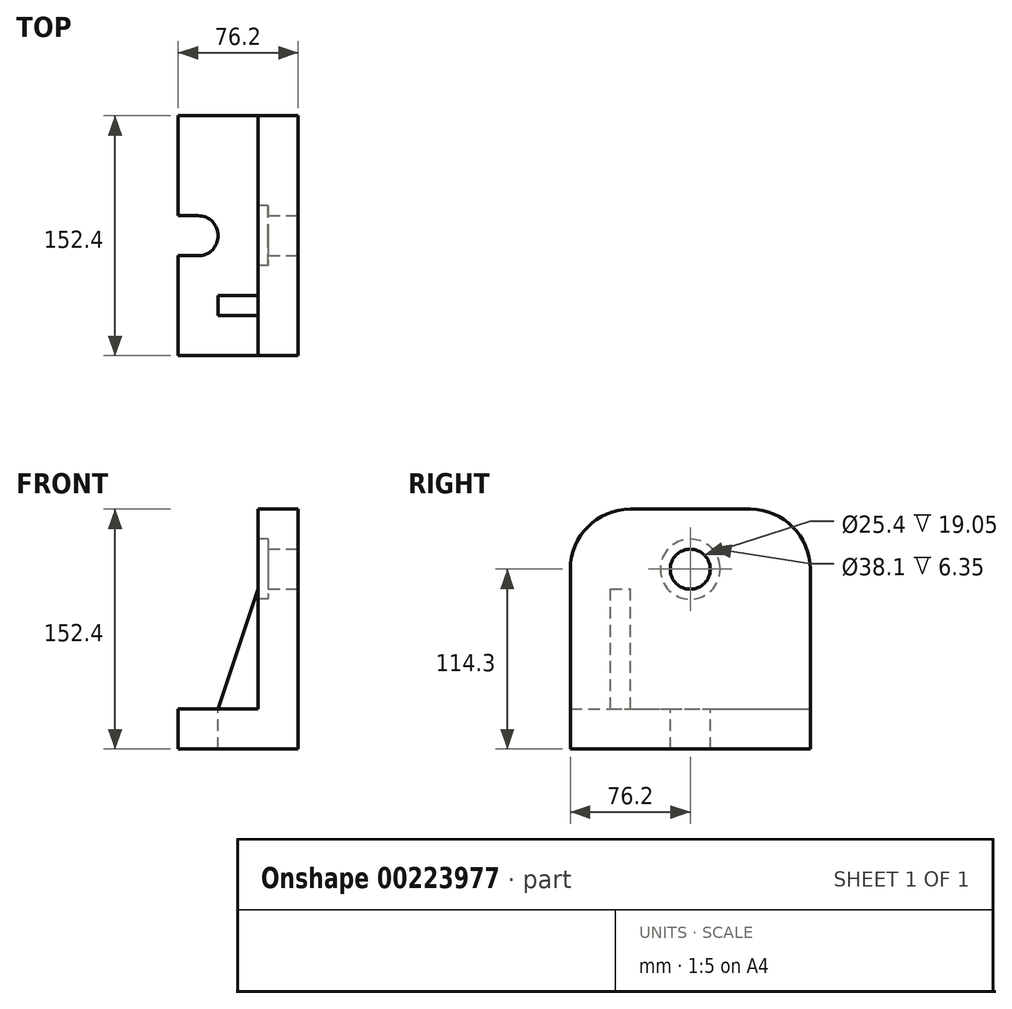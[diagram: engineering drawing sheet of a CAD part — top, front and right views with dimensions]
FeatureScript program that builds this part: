
annotation { "Feature Type Name" : "Feature", "Feature Type Description" : "" }
export const myFeature = defineFeature(function(context is Context, id is Id, definition is map)
    precondition{}
    {
        {
            var Q0;
            Q0=qCreatedBy(makeId("Front.planeOp"),FACE);
            var sketch = newSketch(context, id + "F0", { "sketchPlane" : qUnion([Q0])});
            skLineSegment(sketch, "E0", {"start": v(0, 0) * mm, "end": v(-76.2, 0) * mm});
            skLineSegment(sketch, "E1", {"start": v(-76.2, 0) * mm, "end": v(-76.2, 25.4) * mm});
            skLineSegment(sketch, "E2", {"start": v(-76.2, 25.4) * mm, "end": v(-25.4, 25.4) * mm});
            skLineSegment(sketch, "E3", {"start": v(-25.4, 25.4) * mm, "end": v(-25.4, 152.4) * mm});
            skLineSegment(sketch, "E4", {"start": v(-25.4, 152.4) * mm, "end": v(0, 152.4) * mm});
            skLineSegment(sketch, "E5", {"start": v(0, 152.4) * mm, "end": v(0, 0) * mm});
            skSolve(sketch);
        }
        {
            var Q0;
            Q0 = qSketchRegion(id + "F0", true);
            extrude(context, id + "F1", {"entities" : qUnion([Q0]), "endBound" : BoundingType.SYMMETRIC, "depth" : 152.4 * mm});
        }
        {
            var Q0;
            Q0=makeQuery(id+"F1.opExtrude","SWEPT_FACE",FACE,{"disambiguationData":[OSD([sQuery(id+"F0.wireOp",EDGE,"E5")])]});
            var sketch = newSketch(context, id + "F2", { "sketchPlane" : qUnion([Q0])});
            skCircle(sketch, "E6", {"center": v(0, 114.3) * mm, "radius": 12.7 * mm});
            skSolve(sketch);
        }
        {
            var Q0;
            Q0=makeQuery(id+"F2.imprint","IMPRINT",FACE,{"disambiguationData":[TD([[makeQuery(id+"F2.imprint","IMPRINT",EDGE,{"derivedFrom":sQuery(id+"F2.wireOp",EDGE,"E6")}),1.0]])]});
            extrude(context, id + "F3", {"entities" : qUnion([Q0]), "operationType" : NewBodyOperationType.REMOVE, "endBound" : BoundingType.THROUGH_ALL, "oppositeDirection" : true, "depth" : 25.4 * mm});
        }
        {
            var Q0;
            Q0=makeQuery(id+"F1.opExtrude","SWEPT_FACE",FACE,{"disambiguationData":[OSD([sQuery(id+"F0.wireOp",EDGE,"E2")])]});
            var sketch = newSketch(context, id + "F4", { "sketchPlane" : qUnion([Q0])});
            skLineSegment(sketch, "E7", {"start": v(-76.2, 12.7) * mm, "end": v(-63.5, 12.7) * mm});
            skLineSegment(sketch, "E8", {"start": v(-63.5, -12.7) * mm, "end": v(-76.2, -12.7) * mm});
            skArc(sketch, "E9", {"start": v(-63.5, -12.7) * mm, "mid": v(-50.8, 0) * mm, "end": v(-63.5, 12.7) * mm});
            skSolve(sketch);
        }
        {
            var Q0;
            {var subQ0=sQuery(id+"F4.wireOp",EDGE,"E7");Q0=makeQuery(id+"F4.imprint","IMPRINT",FACE,{"disambiguationData":[TD([[makeQuery(id+"F4.imprint","IMPRINT",EDGE,{"derivedFrom":subQ0}),-1.0]])]});}
            extrude(context, id + "F5", {"entities" : qUnion([Q0]), "operationType" : NewBodyOperationType.REMOVE, "endBound" : BoundingType.THROUGH_ALL, "oppositeDirection" : true, "depth" : 25.4 * mm});
        }
        {
            var Q0;
            Q0=makeQuery(id+"F1.opExtrude","CAP_EDGE",EDGE,{"disambiguationData":[OSD([sQuery(id+"F0.wireOp",EDGE,"E4")])],"isStart":false});
            var Q1;
            Q1=makeQuery(id+"F1.opExtrude","CAP_EDGE",EDGE,{"disambiguationData":[OSD([sQuery(id+"F0.wireOp",EDGE,"E4")])],"isStart":true});
            fillet(context, id + "F6", {"entities" : qUnion([Q0, Q1]), "radius" : 38.1 * mm, "tangentPropagation" : true, "allowEdgeOverflow" : false});
        }
        {
            var Q0;
            Q0=makeQuery(id+"F1.opExtrude","SWEPT_FACE",FACE,{"disambiguationData":[OSD([sQuery(id+"F0.wireOp",EDGE,"E3")])]});
            var sketch = newSketch(context, id + "F7", { "sketchPlane" : qUnion([Q0])});
            skCircle(sketch, "E10", {"center": v(0, 114.3) * mm, "radius": 19.05 * mm});
            skSolve(sketch);
        }
        {
            var Q0;
            Q0=makeQuery(id+"F7.imprint","IMPRINT",FACE,{"disambiguationData":[TD([[makeQuery(id+"F7.imprint","IMPRINT",EDGE,{"derivedFrom":sQuery(id+"F7.wireOp",EDGE,"E10")}),1.0]])]});
            extrude(context, id + "F8", {"entities" : qUnion([Q0]), "operationType" : NewBodyOperationType.REMOVE, "oppositeDirection" : true, "depth" : 6.35 * mm});
        }
        {
            var Q0;
            Q0=qCreatedBy(makeId("Front.planeOp"),FACE);
            cPlane(context, id + "F9", {"entities" : qUnion([Q0]), "cplaneType" : CPlaneType.OFFSET, "offset" : 44.45 * mm, "width" : 152.4 * mm, "height" : 152.4 * mm});
        }
        {
            var Q0;
            Q0=qCreatedBy(id+"F9.planeOp",FACE);
            var sketch = newSketch(context, id + "F10", { "sketchPlane" : qUnion([Q0])});
            skLineSegment(sketch, "E11.0", {"start": v(-25.4, 25.4) * mm, "end": v(-25.4, 101.6) * mm});
            skLineSegment(sketch, "E12.0", {"start": v(-50.8, 25.4) * mm, "end": v(-25.4, 25.4) * mm});
            skLineSegment(sketch, "E13", {"start": v(-25.4, 101.6) * mm, "end": v(-50.8, 25.4) * mm});
            skSolve(sketch);
        }
        {
            var Q0;
            Q0=makeQuery(id+"F10.imprint","IMPRINT",FACE,{"disambiguationData":[TD([[makeQuery(id+"F10.imprint","IMPRINT",EDGE,{"derivedFrom":sQuery(id+"F10.wireOp",EDGE,"E11.0")}),1.0]])]});
            extrude(context, id + "F11", {"entities" : qUnion([Q0]), "operationType" : NewBodyOperationType.ADD, "endBound" : BoundingType.SYMMETRIC, "depth" : 12.7 * mm});
        }
    });
